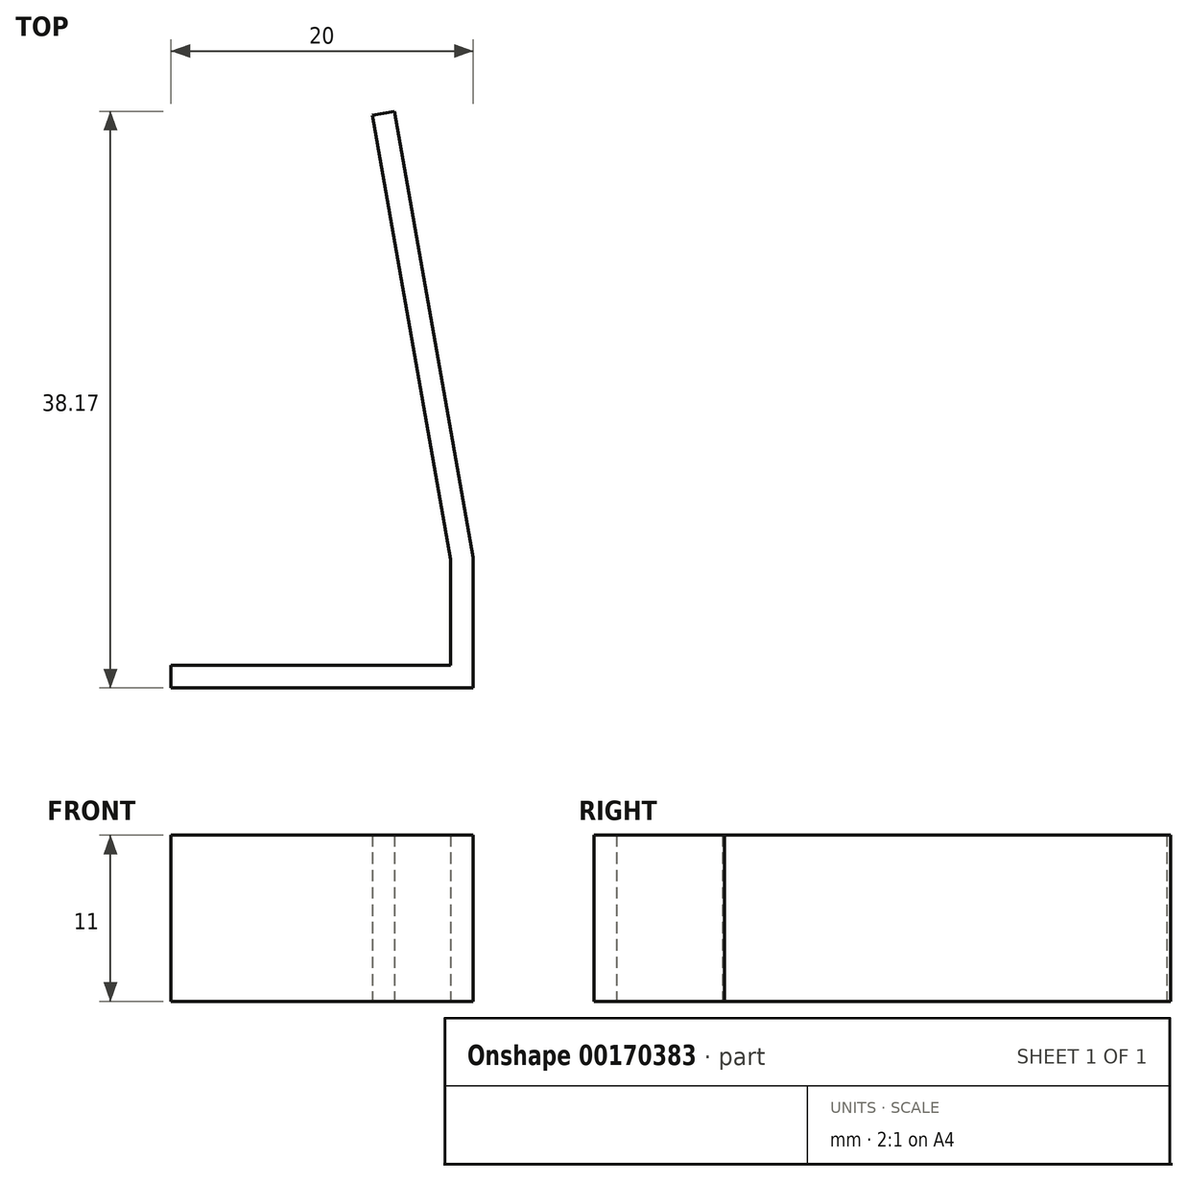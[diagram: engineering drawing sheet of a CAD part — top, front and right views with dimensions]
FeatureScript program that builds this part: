
annotation { "Feature Type Name" : "Feature", "Feature Type Description" : "" }
export const myFeature = defineFeature(function(context is Context, id is Id, definition is map)
    precondition{}
    {
        {
            var Q0;
            Q0=qCreatedBy(makeId("Top.planeOp"),FACE);
            var sketch = newSketch(context, id + "F0", { "sketchPlane" : qUnion([Q0])});
            skLineSegment(sketch, "E0", {"start": v(-27.22, -8.63) * mm, "end": v(-7.22, -8.63) * mm});
            skLineSegment(sketch, "E1", {"start": v(-7.22, -8.63) * mm, "end": v(-7.22, 0) * mm});
            skLineSegment(sketch, "E2", {"start": v(-7.22, 0) * mm, "end": v(-12.43, 29.54) * mm});
            skLineSegment(sketch, "E3", {"start": v(-12.43, 29.54) * mm, "end": v(-13.9, 29.28) * mm});
            skLineSegment(sketch, "E4", {"start": v(-13.9, 29.28) * mm, "end": v(-8.72, -0.13) * mm});
            skLineSegment(sketch, "E5", {"start": v(-8.72, -0.13) * mm, "end": v(-8.72, -7.13) * mm});
            skLineSegment(sketch, "E6", {"start": v(-8.72, -7.13) * mm, "end": v(-27.22, -7.13) * mm});
            skLineSegment(sketch, "E7.direction1", {"start": v(-7.22, -8.63) * mm, "end": v(-21.22, -8.63) * mm, "construction": true});
            skLineSegment(sketch, "E8", {"start": v(-27.22, -7.13) * mm, "end": v(-27.22, -8.63) * mm});
            skSolve(sketch);
        }
        {
            var Q0;
            Q0 = qSketchRegion(id + "F0", true);
            extrude(context, id + "F1", {"entities" : qUnion([Q0]), "depth" : 11 * mm});
        }
    });
